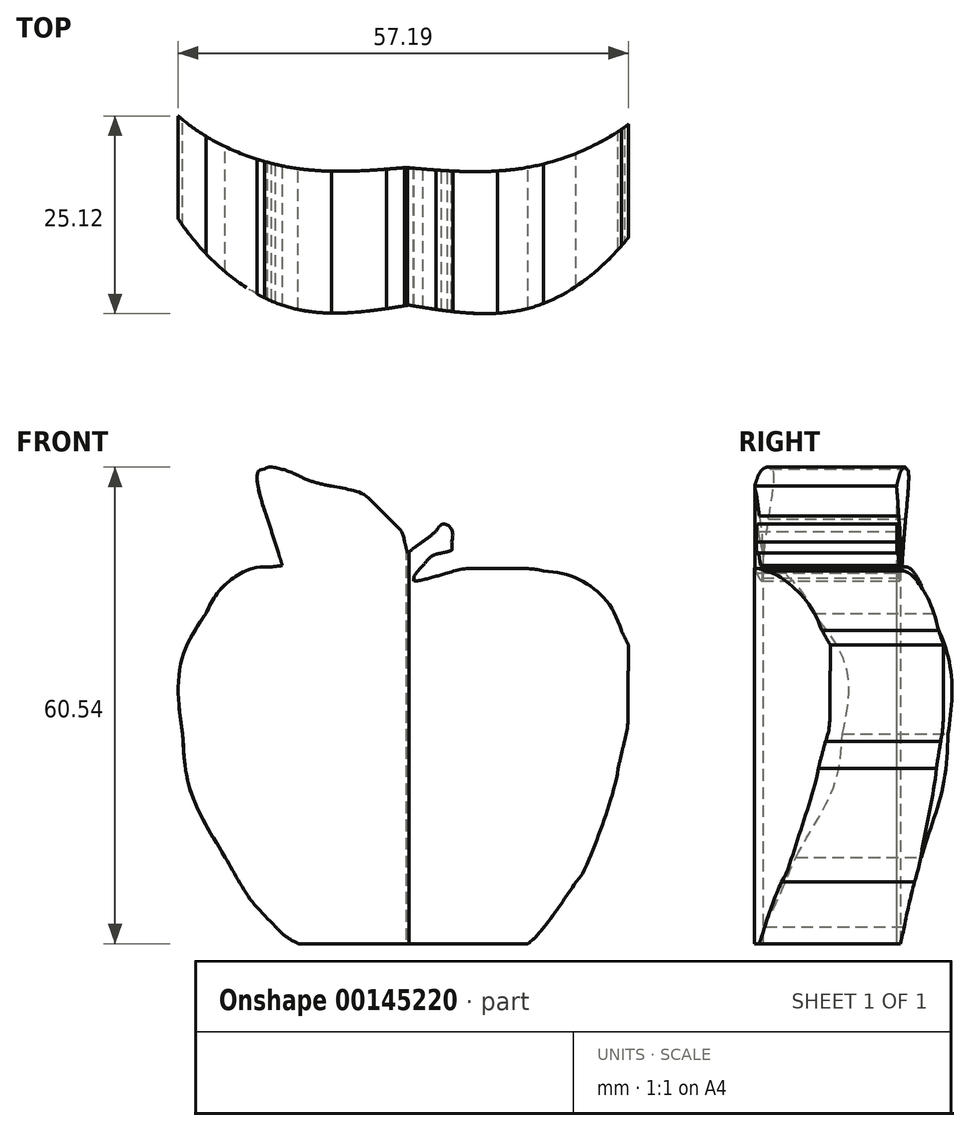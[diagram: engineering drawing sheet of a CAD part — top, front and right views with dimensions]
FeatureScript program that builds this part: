
annotation { "Feature Type Name" : "Feature", "Feature Type Description" : "" }
export const myFeature = defineFeature(function(context is Context, id is Id, definition is map)
    precondition{}
    {
        {
            var Q0;
            Q0=qCreatedBy(makeId("Top.planeOp"),FACE);
            var sketch = newSketch(context, id + "F0", { "sketchPlane" : qUnion([Q0])});
            skFitSpline(sketch, "E0", {"points": [v(-51.73, 51.47) * mm, v(-59.44, 40.77) * mm, v(-73.66, 34.17) * mm, v(-89.05, 34.16) * mm]});
            skFitSpline(sketch, "E1", {"points": [v(-89.05, 34.16) * mm, v(-103.68, 34.16) * mm, v(-117.3, 40.12) * mm, v(-125.27, 50) * mm]});
            skFitSpline(sketch, "E2", {"points": [v(-125.27, 50) * mm, v(-119.42, 29.93) * mm, v(-104.9, 16.7) * mm, v(-88.7, 16.68) * mm]});
            skFitSpline(sketch, "E3", {"points": [v(-88.7, 16.68) * mm, v(-72.08, 16.7) * mm, v(-57.26, 30.64) * mm, v(-51.73, 51.47) * mm]});
            skSolve(sketch);
        }
        {
            var Q0;
            Q0=makeQuery(id+"F0.imprint","IMPRINT",FACE,{"disambiguationData":[TD([[makeQuery(id+"F0.imprint","IMPRINT",EDGE,{"derivedFrom":sQuery(id+"F0.wireOp",EDGE,"E0")}),1.0]])]});
            var Q1;
            Q1=sQuery(id+"F0.wireOp",EDGE,"E0");
            var Q2;
            Q2=sQuery(id+"F0.wireOp",EDGE,"E1");
            var Q3;
            Q3=sQuery(id+"F0.wireOp",EDGE,"E2");
            var Q4;
            Q4=sQuery(id+"F0.wireOp",EDGE,"E3");
            extrude(context, id + "F1", {"entities" : qUnion([Q0]), "surfaceEntities" : qUnion([Q1, Q2, Q3, Q4]), "depth" : 70 * mm});
        }
        {
            var Q0;
            Q0=qCreatedBy(makeId("Front.planeOp"),FACE);
            cPlane(context, id + "F2", {"entities" : qUnion([Q0]), "cplaneType" : CPlaneType.OFFSET, "offset" : 25 * mm, "oppositeDirection" : true, "width" : 150 * mm, "height" : 150 * mm});
        }
        {
            var Q0;
            Q0=qCreatedBy(id+"F2.planeOp",FACE);
            var sketch = newSketch(context, id + "F3", { "sketchPlane" : qUnion([Q0])});
            skFitSpline(sketch, "E4", {"points": [v(-91.38, -1.28) * mm, v(-91.88, -0.93) * mm, v(-92.2, -0.9) * mm, v(-93.06, -1.13) * mm]});
            skFitSpline(sketch, "E5", {"points": [v(-93.06, -1.13) * mm, v(-94.64, -1.57) * mm, v(-98.05, -1.5) * mm, v(-99.86, -0.98) * mm]});
            skFitSpline(sketch, "E6", {"points": [v(-99.86, -0.98) * mm, v(-101.8, -0.42) * mm, v(-104.57, 1.1) * mm, v(-105.6, 2.16) * mm]});
            skFitSpline(sketch, "E7", {"points": [v(-105.6, 2.16) * mm, v(-108.3, 4.94) * mm, v(-109.52, 6.61) * mm, v(-112.03, 10.98) * mm]});
            skFitSpline(sketch, "E8", {"points": [v(-112.03, 10.98) * mm, v(-115.37, 16.79) * mm, v(-116.92, 21.27) * mm, v(-117.44, 26.64) * mm]});
            skFitSpline(sketch, "E9", {"points": [v(-117.44, 26.64) * mm, v(-118, 32.52) * mm, v(-117.02, 37.61) * mm, v(-114.48, 41.94) * mm]});
            skFitSpline(sketch, "E10", {"points": [v(-114.48, 41.94) * mm, v(-112.76, 44.86) * mm, v(-109.02, 47.52) * mm, v(-106.15, 47.86) * mm]});
            skLineSegment(sketch, "E11", {"start": v(-106.15, 47.86) * mm, "end": v(-104.77, 48.03) * mm});
            skLineSegment(sketch, "E12", {"start": v(-104.77, 48.03) * mm, "end": v(-105.27, 49.62) * mm});
            skFitSpline(sketch, "E13", {"points": [v(-105.27, 49.62) * mm, v(-105.55, 50.49) * mm, v(-106.17, 52.45) * mm, v(-106.65, 53.97) * mm]});
            skFitSpline(sketch, "E14", {"points": [v(-106.65, 53.97) * mm, v(-107.67, 57.18) * mm, v(-107.85, 59.99) * mm, v(-107.06, 60.3) * mm]});
            skFitSpline(sketch, "E15", {"points": [v(-107.06, 60.3) * mm, v(-106.42, 60.53) * mm, v(-103.94, 60) * mm, v(-102.32, 59.25) * mm]});
            skFitSpline(sketch, "E16", {"points": [v(-102.32, 59.25) * mm, v(-101.6, 58.92) * mm, v(-99.9, 58.41) * mm, v(-98.53, 58.12) * mm]});
            skFitSpline(sketch, "E17", {"points": [v(-98.53, 58.12) * mm, v(-95.27, 57.43) * mm, v(-93.96, 56.71) * mm, v(-91.56, 54.32) * mm]});
            skFitSpline(sketch, "E18", {"points": [v(-91.56, 54.32) * mm, v(-89.95, 52.72) * mm, v(-89.5, 52.07) * mm, v(-89.22, 50.99) * mm]});
            skLineSegment(sketch, "E19", {"start": v(-89.22, 50.99) * mm, "end": v(-88.9, 49.64) * mm});
            skLineSegment(sketch, "E20", {"start": v(-88.9, 49.64) * mm, "end": v(-87.27, 50.83) * mm});
            skFitSpline(sketch, "E21", {"points": [v(-87.27, 50.83) * mm, v(-86.38, 51.48) * mm, v(-85.49, 52.19) * mm, v(-85.28, 52.39) * mm]});
            skFitSpline(sketch, "E22", {"points": [v(-85.28, 52.39) * mm, v(-84.34, 53.32) * mm, v(-83.26, 52.58) * mm, v(-83.26, 51) * mm]});
            skFitSpline(sketch, "E23", {"points": [v(-83.26, 51) * mm, v(-83.26, 49.98) * mm, v(-83.3, 49.93) * mm, v(-84.53, 49.62) * mm]});
            skFitSpline(sketch, "E24", {"points": [v(-84.53, 49.62) * mm, v(-85.48, 49.38) * mm, v(-86.1, 48.97) * mm, v(-86.93, 48.02) * mm]});
            skFitSpline(sketch, "E25", {"points": [v(-86.93, 48.02) * mm, v(-87.55, 47.32) * mm, v(-88.05, 46.63) * mm, v(-88.05, 46.48) * mm]});
            skFitSpline(sketch, "E26", {"points": [v(-88.05, 46.48) * mm, v(-88.05, 46.12) * mm, v(-86.43, 46.35) * mm, v(-83.82, 47.07) * mm]});
            skFitSpline(sketch, "E27", {"points": [v(-83.82, 47.07) * mm, v(-82.1, 47.55) * mm, v(-80.9, 47.67) * mm, v(-77.41, 47.67) * mm]});
            skFitSpline(sketch, "E28", {"points": [v(-77.41, 47.67) * mm, v(-75.05, 47.67) * mm, v(-72.45, 47.53) * mm, v(-71.63, 47.36) * mm]});
            skFitSpline(sketch, "E29", {"points": [v(-71.63, 47.36) * mm, v(-67.63, 46.53) * mm, v(-63.41, 43.3) * mm, v(-61.7, 39.77) * mm]});
            skLineSegment(sketch, "E30", {"start": v(-61.7, 39.77) * mm, "end": v(-60.82, 37.94) * mm});
            skLineSegment(sketch, "E31", {"start": v(-60.82, 37.94) * mm, "end": v(-60.85, 32.72) * mm});
            skFitSpline(sketch, "E32", {"points": [v(-60.85, 32.72) * mm, v(-60.87, 29.02) * mm, v(-61, 26.96) * mm, v(-61.32, 25.66) * mm]});
            skFitSpline(sketch, "E33", {"points": [v(-61.32, 25.66) * mm, v(-61.57, 24.65) * mm, v(-61.92, 23.13) * mm, v(-62.11, 22.27) * mm]});
            skFitSpline(sketch, "E34", {"points": [v(-62.11, 22.27) * mm, v(-62.82, 19.09) * mm, v(-66.46, 9.28) * mm, v(-67.47, 7.84) * mm]});
            skFitSpline(sketch, "E35", {"points": [v(-67.47, 7.84) * mm, v(-71, 2.8) * mm, v(-73.68, -0.08) * mm, v(-75.77, -1.05) * mm]});
            skFitSpline(sketch, "E36", {"points": [v(-75.77, -1.05) * mm, v(-77.55, -1.88) * mm, v(-80.92, -1.97) * mm, v(-82.73, -1.24) * mm]});
            skFitSpline(sketch, "E37", {"points": [v(-82.73, -1.24) * mm, v(-83.84, -0.8) * mm, v(-84, -0.8) * mm, v(-85.25, -1.24) * mm]});
            skFitSpline(sketch, "E38", {"points": [v(-85.25, -1.24) * mm, v(-86.99, -1.86) * mm, v(-90.51, -1.88) * mm, v(-91.38, -1.28) * mm]});
            skSolve(sketch);
        }
        {
            var Q0;
            Q0=makeQuery(id+"F3.imprint","IMPRINT",FACE,{"disambiguationData":[TD([[makeQuery(id+"F3.imprint","IMPRINT",EDGE,{"derivedFrom":sQuery(id+"F3.wireOp",EDGE,"E4")}),-1.0]])]});
            var Q1;
            Q1=sQuery(id+"F3.wireOp",EDGE,"E8");
            var Q2;
            Q2=sQuery(id+"F3.wireOp",EDGE,"E9");
            var Q3;
            Q3=sQuery(id+"F3.wireOp",EDGE,"E10");
            var Q4;
            Q4=sQuery(id+"F3.wireOp",EDGE,"E13");
            var Q5;
            Q5=sQuery(id+"F3.wireOp",EDGE,"E12");
            var Q6;
            Q6=sQuery(id+"F3.wireOp",EDGE,"E11");
            var Q7;
            Q7=sQuery(id+"F3.wireOp",EDGE,"E14");
            var Q8;
            Q8=sQuery(id+"F3.wireOp",EDGE,"E15");
            var Q9;
            Q9=sQuery(id+"F3.wireOp",EDGE,"E16");
            var Q10;
            Q10=sQuery(id+"F3.wireOp",EDGE,"E17");
            var Q11;
            Q11=sQuery(id+"F3.wireOp",EDGE,"E19");
            var Q12;
            Q12=sQuery(id+"F3.wireOp",EDGE,"E18");
            var Q13;
            Q13=sQuery(id+"F3.wireOp",EDGE,"E20");
            var Q14;
            Q14=sQuery(id+"F3.wireOp",EDGE,"E21");
            var Q15;
            Q15=sQuery(id+"F3.wireOp",EDGE,"E20");
            var Q16;
            Q16=sQuery(id+"F3.wireOp",EDGE,"E22");
            var Q17;
            Q17=sQuery(id+"F3.wireOp",EDGE,"E23");
            var Q18;
            Q18=sQuery(id+"F3.wireOp",EDGE,"E24");
            var Q19;
            Q19=sQuery(id+"F3.wireOp",EDGE,"E25");
            var Q20;
            Q20=sQuery(id+"F3.wireOp",EDGE,"E26");
            var Q21;
            Q21=sQuery(id+"F3.wireOp",EDGE,"E27");
            var Q22;
            Q22=sQuery(id+"F3.wireOp",EDGE,"E28");
            var Q23;
            Q23=sQuery(id+"F3.wireOp",EDGE,"E29");
            var Q24;
            Q24=sQuery(id+"F3.wireOp",EDGE,"E28");
            var Q25;
            Q25=sQuery(id+"F3.wireOp",EDGE,"E30");
            var Q26;
            Q26=sQuery(id+"F3.wireOp",EDGE,"E31");
            var Q27;
            Q27=sQuery(id+"F3.wireOp",EDGE,"E33");
            var Q28;
            Q28=sQuery(id+"F3.wireOp",EDGE,"E32");
            var Q29;
            Q29=sQuery(id+"F3.wireOp",EDGE,"E34");
            var Q30;
            Q30=sQuery(id+"F3.wireOp",EDGE,"E35");
            var Q31;
            Q31=sQuery(id+"F3.wireOp",EDGE,"E36");
            var Q32;
            Q32=sQuery(id+"F3.wireOp",EDGE,"E37");
            var Q33;
            Q33=sQuery(id+"F3.wireOp",EDGE,"E38");
            var Q34;
            Q34=sQuery(id+"F3.wireOp",EDGE,"E4");
            var Q35;
            Q35=sQuery(id+"F3.wireOp",EDGE,"E5");
            var Q36;
            Q36=sQuery(id+"F3.wireOp",EDGE,"E6");
            var Q37;
            Q37=sQuery(id+"F3.wireOp",EDGE,"E7");
            extrude(context, id + "F4", {"entities" : qUnion([Q0]), "operationType" : NewBodyOperationType.INTERSECT, "surfaceEntities" : qUnion([Q1, Q2, Q3, Q4, Q5, Q6, Q7, Q8, Q9, Q10, Q11, Q12, Q13, Q14, Q15, Q16, Q17, Q18, Q19, Q20, Q21, Q22, Q23, Q24, Q25, Q26, Q27, Q28, Q29, Q30, Q31, Q32, Q33, Q34, Q35, Q36, Q37]), "endBound" : BoundingType.THROUGH_ALL, "depth" : 25 * mm, "hasSecondDirection" : true, "secondDirectionBound" : SecondDirectionBoundingType.THROUGH_ALL, "secondDirectionOppositeDirection" : true, "secondDirectionDepth" : 25 * mm});
        }
    });
